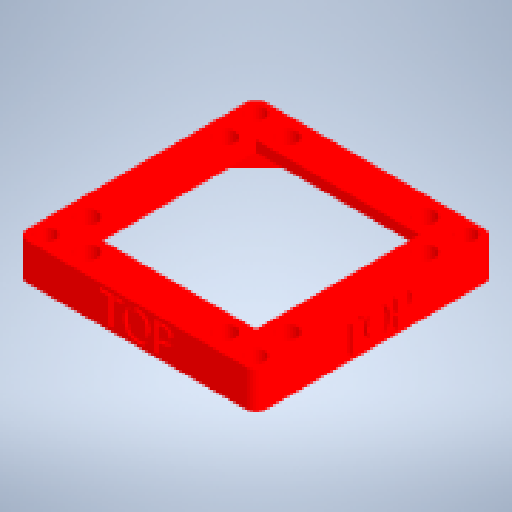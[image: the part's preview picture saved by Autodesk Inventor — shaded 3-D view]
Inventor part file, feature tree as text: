
AUTODESK INVENTOR PART (.ipt)
format: ipt  version: 2023.1 (Build 271208000, 208)  size: 577,024 bytes
history: native  units: mm
features: extrude x5, sketch x2, chamfer x2, fillet x1, pattern_circular x1, projected_geometry x1
ambient origin geometry x8: Origin, YZ Plane, XZ Plane, XY Plane, X Axis, Y Axis, Z Axis, Center Point
bodies: Solid1 (feature_tree)
feature tree (12):
  sketch  "Sketch1"  dims[d0=49.8mm d1=49.8mm]
  extrude  "Extrusion1"  Depth=49.8mm
  extrude  "Extrusion2"  Depth=3.0mm
  chamfer  "Chamfer1"  Distance=3.0mm
  fillet  "Fillet1"  Radius=3.75mm
  chamfer  "Chamfer2"  Distance=4.2125mm
  extrude  "Extrusion3"  Depth=0.675mm
  extrude  "Extrusion4"  Depth=10.5mm
  extrude  "Extrusion5"  Depth=10.5mm
  pattern_circular  "Circular Pattern1"  [2 undecoded]
  sketch  "Sketch2"  dims[d2=7.85mm d3=3.0mm d4=3.0mm d5=3.75mm d6=4.2125mm d7=0.675mm d8=10.5mm d9=10.5mm d10=4.1mm d11=4.14675mm d12=7.85mm d13=7.85mm d14=5.5mm d15=5.5mm d16=40.0mm d18=360.0deg d20=7.7mm d21=0.0mm d22=2.2mm d23=0.0mm d24=5.5mm d25=2.0mm d26=45.0deg d27=2.0mm d28=0.025mm d29=2.0mm d30=45.0deg d31=3.0mm d32=0.0mm d33=3.0mm d34=0.0mm d35=0.75mm d36=0.0mm d37=40.0mm d38=360.0deg]
  projected_geometry  "Projected Loop2"
note: 2 required parameter values undecoded (feature->parameter linkage not recoverable at this tier; creation-order binding heuristic only, values carry confidence <= 0.55)
